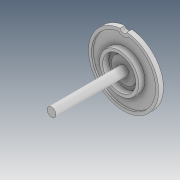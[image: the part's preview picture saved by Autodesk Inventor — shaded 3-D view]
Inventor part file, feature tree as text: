
AUTODESK INVENTOR PART (.ipt)
format: ipt  version: 2020 (Build 240168000, 168)  size: 150,016 bytes
history: native  units: mm
features: extrude x8, sketch x8, plane x2
ambient origin geometry x8: Origin, YZ Plane, XZ Plane, XY Plane, X Axis, Y Axis, Z Axis, Center Point
bodies: Solid1 (feature_tree)
feature tree (18):
  extrude  "Extrusion1"  Depth=1.0mm TaperAngle=0.0deg
  plane  "Work Plane1"
  extrude  "Extrusion3"  Depth=10.75mm
  plane  "Work Plane2"
  extrude  "Extrusion5"  Depth=2.0mm
  extrude  "Extrusion6"  Depth=0.4mm
  extrude  "Pressguide"  Depth=10.0mm
  extrude  "Extrusion8"  Depth=3.0mm
  extrude  "Extrusion9"  Depth=3.0mm TaperAngle=0.0deg
  extrude  "Axle"  Depth=0.57mm TaperAngle=0.0deg
  sketch  "Sketch1"  dims[d0=22.8mm d1=1.0mm d2=0.0mm]
  sketch  "Sketch3"  dims[d6=12.75mm d7=10.75mm]
  sketch  "Sketch5"  dims[d8=2.0mm d9=0.0mm d14=8.25mm]
  sketch  "Sketch6"  dims[d15=0.4mm d16=0.0mm d17=2.9mm]
  sketch  "Sketch7"  dims[d18=10.0mm d19=0.0mm d20=5.0mm]
  sketch  "Sketch8"  dims[d21=3.0mm d22=0.0mm d23=2.2mm]
  sketch  "Sketch9"  dims[d24=0.8mm d25=3.0mm d26=0.0mm]
  sketch  "Sketch10"  dims[d27=1.0mm d28=0.57mm d29=0.0mm d30=25.0mm d31=0.0mm]
